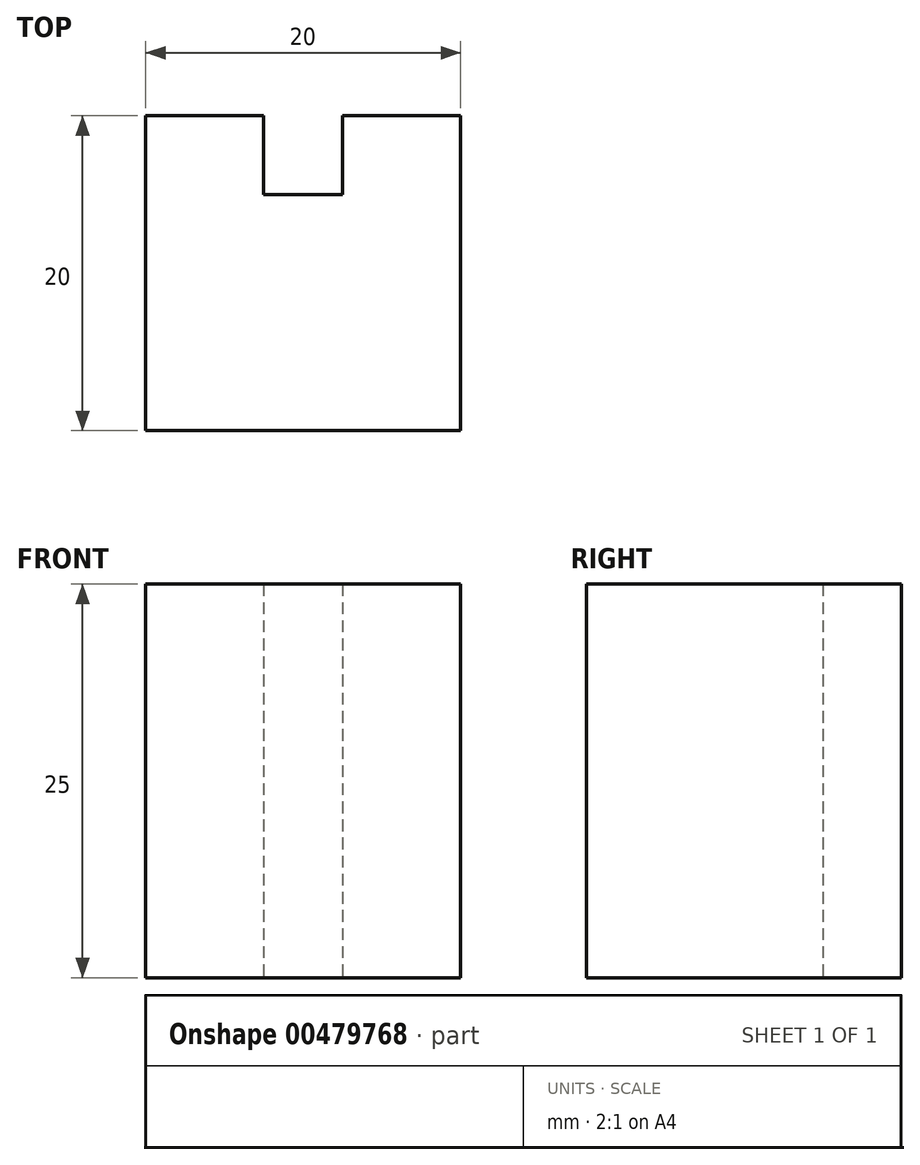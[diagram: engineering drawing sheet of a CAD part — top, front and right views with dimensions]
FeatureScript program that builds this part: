
annotation { "Feature Type Name" : "Feature", "Feature Type Description" : "" }
export const myFeature = defineFeature(function(context is Context, id is Id, definition is map)
    precondition{}
    {
        {
            var Q0;
            Q0=qCreatedBy(makeId("Top.planeOp"),FACE);
            var sketch = newSketch(context, id + "F0", { "sketchPlane" : qUnion([Q0])});
            skLineSegment(sketch, "E0.bottom", {"start": v(0, 0) * mm, "end": v(20, 0) * mm});
            skLineSegment(sketch, "E0.left", {"start": v(0, 0) * mm, "end": v(0, 20) * mm});
            skLineSegment(sketch, "E0.right", {"start": v(20, 0) * mm, "end": v(20, 20) * mm});
            skLineSegment(sketch, "E1", {"start": v(7.5, 20) * mm, "end": v(7.5, 15) * mm});
            skLineSegment(sketch, "E2", {"start": v(7.5, 15) * mm, "end": v(12.5, 15) * mm});
            skLineSegment(sketch, "E3", {"start": v(12.5, 15) * mm, "end": v(12.5, 20) * mm});
            skLineSegment(sketch, "E4", {"start": v(0, 20) * mm, "end": v(7.5, 20) * mm});
            skLineSegment(sketch, "E5", {"start": v(12.5, 20) * mm, "end": v(20, 20) * mm});
            skSolve(sketch);
        }
        {
            var Q0;
            Q0=makeQuery(id+"F0.imprint","IMPRINT",FACE,{"disambiguationData":[TD([[makeQuery(id+"F0.imprint","IMPRINT",EDGE,{"derivedFrom":sQuery(id+"F0.wireOp",EDGE,"E0.bottom")}),1.0]])]});
            extrude(context, id + "F1", {"entities" : qUnion([Q0]), "depth" : 25 * mm});
        }
    });
